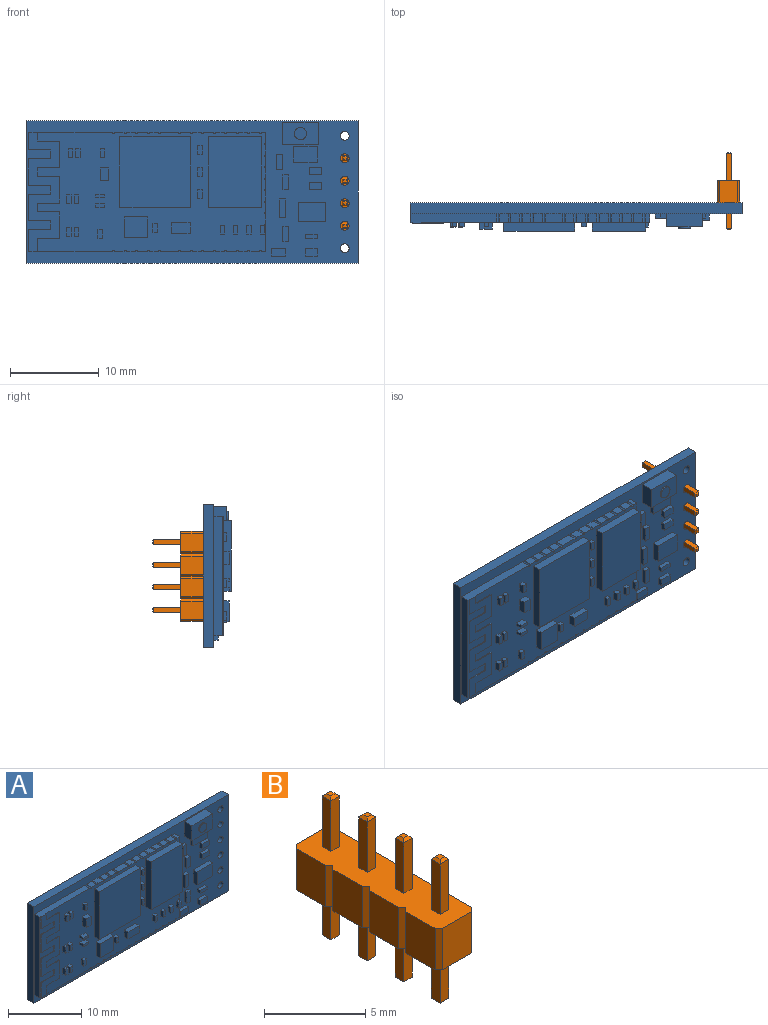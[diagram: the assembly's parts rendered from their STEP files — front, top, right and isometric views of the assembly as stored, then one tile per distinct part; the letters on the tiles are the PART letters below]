
ASSEMBLY  parts=2 mates=1
PART A: 290 faces, bbox 37.5x3.2x16.1 mm
  f0: plane 2.91x1mm, normal (1,0,0), area 2.9mm2, adj f34,f35,f43,f283
  f1: plane 1x1mm, normal (1,0,0), area 1mm2, adj f34,f35,f282,f283
  f2: plane 1x1mm, normal (1,0,0), area 1mm2, adj f34,f35,f281,f282
  f3: plane 1x1mm, normal (1,0,0), area 1mm2, adj f34,f35,f280,f281
  f4: plane 1x1mm, normal (1,0,0), area 1mm2, adj f34,f35,f279,f280
  f5: plane 1x1mm, normal (1,0,0), area 1mm2, adj f34,f35,f278,f279
  f6: plane 1x1mm, normal (1,0,0), area 1mm2, adj f34,f35,f277,f278
  f7: plane 1x1mm, normal (1,0,0), area 1mm2, adj f34,f35,f276,f277
  f8: plane 1x1mm, normal (0,0,-1), area 1mm2, adj f34,f35,f274,f275
  f9: plane 1x1mm, normal (0,0,-1), area 1mm2, adj f34,f35,f273,f274
  f10: plane 1x1mm, normal (0,0,-1), area 1mm2, adj f34,f35,f272,f273
  f11: plane 1x1mm, normal (0,0,-1), area 1mm2, adj f34,f35,f271,f272
  f12: plane 1x1mm, normal (0,0,-1), area 1mm2, adj f34,f35,f270,f271
  f13: plane 1x1mm, normal (0,0,-1), area 1mm2, adj f34,f35,f269,f270
  f14: plane 1x1mm, normal (0,0,-1), area 1mm2, adj f34,f35,f268,f269
  f15: plane 1.96x1mm, normal (0,0,-1), area 2mm2, adj f34,f35,f267,f268
  f16: plane 1x1mm, normal (0,0,-1), area 1mm2, adj f34,f35,f266,f267
  f17: plane 1x1mm, normal (0,0,-1), area 1mm2, adj f34,f35,f265,f266
  f18: plane 1x1mm, normal (0,0,-1), area 1mm2, adj f34,f35,f264,f265
  f19: plane 1x1mm, normal (0,0,-1), area 1mm2, adj f34,f35,f263,f264
  f20: plane 9.67x1.1mm, normal (0,0,-1), area 9.8mm2, adj f34,f35,f36,f42,f46,f71,f72,f263
  f21: plane 1x1mm, normal (0,0,1), area 1mm2, adj f34,f35,f261,f262
  f22: plane 1x1mm, normal (0,0,1), area 1mm2, adj f34,f35,f260,f261
  f23: plane 1x1mm, normal (0,0,1), area 1mm2, adj f34,f35,f259,f260
  f24: plane 1x1mm, normal (0,0,1), area 1mm2, adj f34,f35,f258,f259
  f25: plane 1.96x1mm, normal (0,0,1), area 2mm2, adj f34,f35,f257,f258
  f26: plane 1x1mm, normal (0,0,1), area 1mm2, adj f34,f35,f256,f257
  f27: plane 1x1mm, normal (0,0,1), area 1mm2, adj f34,f35,f255,f256
  f28: plane 1x1mm, normal (0,0,1), area 1mm2, adj f34,f35,f254,f255
  f29: plane 1x1mm, normal (0,0,1), area 1mm2, adj f34,f35,f253,f254
  f30: plane 1x1mm, normal (0,0,1), area 1mm2, adj f34,f35,f252,f253
  f31: plane 1x1mm, normal (0,0,1), area 1mm2, adj f34,f35,f251,f252
  f32: plane 1x1mm, normal (0,0,1), area 1mm2, adj f34,f35,f250,f251
  f33: plane 1x0.5mm, normal (0,0,1), area 0.5mm2, adj f34,f35,f44,f250
  f34: plane 37.5x16.1mm, normal (0,-1,0), area 203.9mm2, adj f0,f1,f2,f3,f4,f5,f6,f7
  f35: plane 25.8x13.5mm, normal (0,-1,0), area 194mm2, adj f0,f1,f2,f3,f4,f5,f6,f7
  f36: plane 13.5x2.7mm, normal (0,-1,0), area 10.2mm2, adj f20,f42,f45,f59,f60,f61,f62,f63
  f37: plane 16.1x1.2mm, normal (-1,0,0), area 19.3mm2, adj f34,f38,f40,f41
  f38: plane 37.5x1.2mm, normal (0,0,-1), area 45mm2, adj f34,f37,f39,f41
  f39: plane 16.1x1.2mm, normal (1,0,0), area 19.3mm2, adj f34,f38,f40,f41
  f40: plane 37.5x1.2mm, normal (0,0,1), area 45mm2, adj f34,f37,f39,f41
  f41: plane 37.5x16.1mm, normal (0,1,0), area 599mm2, adj f37,f38,f39,f40,f284,f285,f286,f287
  f42: plane 13.5x1mm, normal (-1,0,0), area 13.5mm2, adj f20,f34,f36,f45
  f43: plane 1x0.5mm, normal (0,0,-1), area 0.5mm2, adj f0,f34,f35,f275
  f44: plane 1.2x1mm, normal (1,0,0), area 1.2mm2, adj f33,f34,f35,f276
  f45: plane 9.67x1.1mm, normal (0,0,1), area 9.8mm2, adj f34,f35,f36,f42,f58,f59,f72,f262
  f46: plane 1.5x0.1mm, normal (1,0,0), area 0.1mm2, adj f20,f35,f47,f72
  f47: plane 2.5x0.1mm, normal (0,0,-1), area 0.2mm2, adj f35,f46,f48,f72
  f48: plane 3x0.1mm, normal (1,0,0), area 0.3mm2, adj f35,f47,f49,f72
  f49: plane 2.5x0.1mm, normal (0,0,1), area 0.2mm2, adj f35,f48,f50,f72
  f50: plane 1x0.1mm, normal (1,0,0), area 0.1mm2, adj f35,f49,f51,f72
  f51: plane 2.5x0.1mm, normal (0,0,-1), area 0.2mm2, adj f35,f50,f52,f72
  f52: plane 3x0.1mm, normal (1,0,0), area 0.3mm2, adj f35,f51,f53,f72
  f53: plane 2.5x0.1mm, normal (0,0,1), area 0.2mm2, adj f35,f52,f54,f72
  f54: plane 1x0.1mm, normal (1,0,0), area 0.1mm2, adj f35,f53,f55,f72
  f55: plane 2.5x0.1mm, normal (0,0,-1), area 0.2mm2, adj f35,f54,f56,f72
  f56: plane 3x0.1mm, normal (1,0,0), area 0.3mm2, adj f35,f55,f57,f72
  f57: plane 2.5x0.1mm, normal (0,0,1), area 0.2mm2, adj f35,f56,f58,f72
  f58: plane 1x0.1mm, normal (1,0,0), area 0.1mm2, adj f35,f45,f57,f72
  f59: plane 2x0.1mm, normal (-1,0,0), area 0.2mm2, adj f36,f45,f60,f72
  f60: plane 2.5x0.1mm, normal (0,0,-1), area 0.2mm2, adj f36,f59,f61,f72
  f61: plane 1x0.1mm, normal (-1,0,0), area 0.1mm2, adj f36,f60,f62,f72
  f62: plane 2.5x0.1mm, normal (0,0,1), area 0.2mm2, adj f36,f61,f63,f72
  f63: plane 3x0.1mm, normal (-1,0,0), area 0.3mm2, adj f36,f62,f64,f72
  f64: plane 2.5x0.1mm, normal (0,0,-1), area 0.2mm2, adj f36,f63,f65,f72
  f65: plane 1x0.1mm, normal (-1,0,0), area 0.1mm2, adj f36,f64,f66,f72
  f66: plane 2.5x0.1mm, normal (0,0,1), area 0.2mm2, adj f36,f65,f67,f72
  f67: plane 3x0.1mm, normal (-1,0,0), area 0.3mm2, adj f36,f66,f68,f72
  f68: plane 2.5x0.1mm, normal (0,0,-1), area 0.2mm2, adj f36,f67,f69,f72
  f69: plane 1x0.1mm, normal (-1,0,0), area 0.1mm2, adj f36,f68,f70,f72
  f70: plane 2.5x0.1mm, normal (0,0,1), area 0.2mm2, adj f36,f69,f71,f72
  f71: plane 2.5x0.1mm, normal (-1,0,0), area 0.2mm2, adj f20,f36,f70,f72
  f72: plane 13.5x3.5mm, normal (0,-1,0), area 28.5mm2, adj f20,f45,f46,f47,f48,f49,f50,f51
  f73: plane 2.5x1.5mm, normal (-1,0,0), area 3.8mm2, adj f34,f74,f76,f77
  f74: plane 4x1.5mm, normal (0,0,-1), area 6mm2, adj f34,f73,f75,f77
  f75: plane 2.5x1.5mm, normal (1,0,0), area 3.8mm2, adj f34,f74,f76,f77
  f76: plane 4x1.5mm, normal (0,0,1), area 6mm2, adj f34,f73,f75,f77
  f77: plane 4x2.5mm, normal (0,-1,0), area 8.5mm2, adj f73,f74,f75,f76,f78
  f78: cylinder r=0.69mm len=1.39mm, axis (0,1,0), area 0.9mm2, adj f77,f79
  f79: plane 1.39x1.39mm, normal (0,-1,0), area 1.5mm2, adj f78
  f80: plane 8x1mm, normal (1,0,0), area 8mm2, adj f35,f81,f83,f84
  f81: plane 6x1mm, normal (0,0,1), area 6mm2, adj f35,f80,f82,f84
  f82: plane 8x1mm, normal (-1,0,0), area 8mm2, adj f35,f81,f83,f84
  f83: plane 6x1mm, normal (0,0,-1), area 6mm2, adj f35,f80,f82,f84
  f84: plane 8x6mm, normal (0,-1,0), area 48mm2, adj f80,f81,f82,f83
  f85: plane 8x1mm, normal (1,0,0), area 8mm2, adj f35,f86,f88,f89
  f86: plane 8x1mm, normal (0,0,1), area 8mm2, adj f35,f85,f87,f89
  f87: plane 8x1mm, normal (-1,0,0), area 8mm2, adj f35,f86,f88,f89
  f88: plane 8x1mm, normal (0,0,-1), area 8mm2, adj f35,f85,f87,f89
  f89: plane 8x8mm, normal (0,-1,0), area 64mm2, adj f85,f86,f87,f88
  f90: plane 1x0.5mm, normal (-1,0,0), area 0.5mm2, adj f35,f91,f93,f94
  f91: plane 0.5x0.5mm, normal (0,0,-1), area 0.3mm2, adj f35,f90,f92,f94
  f92: plane 1x0.5mm, normal (1,0,0), area 0.5mm2, adj f35,f91,f93,f94
  f93: plane 0.5x0.5mm, normal (0,0,1), area 0.3mm2, adj f35,f90,f92,f94
  f94: plane 1x0.5mm, normal (0,-1,0), area 0.5mm2, adj f90,f91,f92,f93
  f95: plane 1x0.5mm, normal (-1,0,0), area 0.5mm2, adj f35,f96,f98,f99
  f96: plane 0.5x0.5mm, normal (0,0,-1), area 0.3mm2, adj f35,f95,f97,f99
  f97: plane 1x0.5mm, normal (1,0,0), area 0.5mm2, adj f35,f96,f98,f99
  f98: plane 0.5x0.5mm, normal (0,0,1), area 0.3mm2, adj f35,f95,f97,f99
  f99: plane 1x0.5mm, normal (0,-1,0), area 0.5mm2, adj f95,f96,f97,f98
  f100: plane 1x0.5mm, normal (-1,0,0), area 0.5mm2, adj f35,f101,f103,f104
  f101: plane 0.5x0.5mm, normal (0,0,-1), area 0.3mm2, adj f35,f100,f102,f104
  f102: plane 1x0.5mm, normal (1,0,0), area 0.5mm2, adj f35,f101,f103,f104
  f103: plane 0.5x0.5mm, normal (0,0,1), area 0.3mm2, adj f35,f100,f102,f104
  f104: plane 1x0.5mm, normal (0,-1,0), area 0.5mm2, adj f100,f101,f102,f103
  f105: plane 1x0.5mm, normal (-1,0,0), area 0.5mm2, adj f35,f106,f108,f109
  f106: plane 0.5x0.5mm, normal (0,0,-1), area 0.2mm2, adj f35,f105,f107,f109
  f107: plane 1x0.5mm, normal (1,0,0), area 0.5mm2, adj f35,f106,f108,f109
  f108: plane 0.5x0.5mm, normal (0,0,1), area 0.2mm2, adj f35,f105,f107,f109
  f109: plane 1x0.5mm, normal (0,-1,0), area 0.5mm2, adj f105,f106,f107,f108
  f110: plane 1x0.5mm, normal (-1,0,0), area 0.5mm2, adj f35,f111,f113,f114
  f111: plane 0.5x0.5mm, normal (0,0,-1), area 0.2mm2, adj f35,f110,f112,f114
  f112: plane 1x0.5mm, normal (1,0,0), area 0.5mm2, adj f35,f111,f113,f114
  f113: plane 0.5x0.5mm, normal (0,0,1), area 0.2mm2, adj f35,f110,f112,f114
  f114: plane 1x0.5mm, normal (0,-1,0), area 0.5mm2, adj f110,f111,f112,f113
  f115: plane 1x0.5mm, normal (-1,0,0), area 0.5mm2, adj f35,f116,f118,f119
  f116: plane 0.5x0.5mm, normal (0,0,-1), area 0.2mm2, adj f35,f115,f117,f119
  f117: plane 1x0.5mm, normal (1,0,0), area 0.5mm2, adj f35,f116,f118,f119
  f118: plane 0.5x0.5mm, normal (0,0,1), area 0.2mm2, adj f35,f115,f117,f119
  f119: plane 1x0.5mm, normal (0,-1,0), area 0.5mm2, adj f115,f116,f117,f118
  f120: plane 1x0.5mm, normal (-1,0,0), area 0.5mm2, adj f35,f121,f123,f124
  f121: plane 0.5x0.5mm, normal (0,0,-1), area 0.2mm2, adj f35,f120,f122,f124
  f122: plane 1x0.5mm, normal (1,0,0), area 0.5mm2, adj f35,f121,f123,f124
  f123: plane 0.5x0.5mm, normal (0,0,1), area 0.2mm2, adj f35,f120,f122,f124
  f124: plane 1x0.5mm, normal (0,-1,0), area 0.5mm2, adj f120,f121,f122,f123
  f125: plane 1x0.5mm, normal (-1,0,0), area 0.5mm2, adj f35,f126,f128,f129
  f126: plane 0.5x0.5mm, normal (0,0,-1), area 0.3mm2, adj f35,f125,f127,f129
  f127: plane 1x0.5mm, normal (1,0,0), area 0.5mm2, adj f35,f126,f128,f129
  f128: plane 0.5x0.5mm, normal (0,0,1), area 0.3mm2, adj f35,f125,f127,f129
  f129: plane 1x0.5mm, normal (0,-1,0), area 0.5mm2, adj f125,f126,f127,f128
  f130: plane 1x0.5mm, normal (-1,0,0), area 0.5mm2, adj f35,f131,f133,f134
  f131: plane 0.5x0.5mm, normal (0,0,-1), area 0.3mm2, adj f35,f130,f132,f134
  f132: plane 1x0.5mm, normal (1,0,0), area 0.5mm2, adj f35,f131,f133,f134
  f133: plane 0.5x0.5mm, normal (0,0,1), area 0.3mm2, adj f35,f130,f132,f134
  f134: plane 1x0.5mm, normal (0,-1,0), area 0.5mm2, adj f130,f131,f132,f133
  f135: plane 1x0.5mm, normal (-1,0,0), area 0.5mm2, adj f35,f136,f138,f139
  f136: plane 0.5x0.5mm, normal (0,0,-1), area 0.3mm2, adj f35,f135,f137,f139
  f137: plane 1x0.5mm, normal (1,0,0), area 0.5mm2, adj f35,f136,f138,f139
  f138: plane 0.5x0.5mm, normal (0,0,1), area 0.3mm2, adj f35,f135,f137,f139
  f139: plane 1x0.5mm, normal (0,-1,0), area 0.5mm2, adj f135,f136,f137,f138
  f140: plane 1x0.5mm, normal (1,0,0), area 0.5mm2, adj f35,f141,f143,f144
  f141: plane 0.5x0.5mm, normal (0,0,1), area 0.3mm2, adj f35,f140,f142,f144
  f142: plane 1x0.5mm, normal (-1,0,0), area 0.5mm2, adj f35,f141,f143,f144
  f143: plane 0.5x0.5mm, normal (0,0,-1), area 0.3mm2, adj f35,f140,f142,f144
  f144: plane 1x0.5mm, normal (0,-1,0), area 0.5mm2, adj f140,f141,f142,f143
  f145: plane 1x0.5mm, normal (-1,0,0), area 0.5mm2, adj f35,f146,f148,f149
  f146: plane 0.5x0.5mm, normal (0,0,-1), area 0.3mm2, adj f35,f145,f147,f149
  f147: plane 1x0.5mm, normal (1,0,0), area 0.5mm2, adj f35,f146,f148,f149
  f148: plane 0.5x0.5mm, normal (0,0,1), area 0.3mm2, adj f35,f145,f147,f149
  f149: plane 1x0.5mm, normal (0,-1,0), area 0.5mm2, adj f145,f146,f147,f148
  f150: plane 1x0.5mm, normal (-1,0,0), area 0.5mm2, adj f35,f151,f153,f154
  f151: plane 0.5x0.5mm, normal (0,0,-1), area 0.3mm2, adj f35,f150,f152,f154
  f152: plane 1x0.5mm, normal (1,0,0), area 0.5mm2, adj f35,f151,f153,f154
  f153: plane 0.5x0.5mm, normal (0,0,1), area 0.3mm2, adj f35,f150,f152,f154
  f154: plane 1x0.5mm, normal (0,-1,0), area 0.5mm2, adj f150,f151,f152,f153
  f155: plane 1x0.5mm, normal (-1,0,0), area 0.5mm2, adj f35,f156,f158,f159
  f156: plane 0.5x0.5mm, normal (0,0,-1), area 0.3mm2, adj f35,f155,f157,f159
  f157: plane 1x0.5mm, normal (1,0,0), area 0.5mm2, adj f35,f156,f158,f159
  f158: plane 0.5x0.5mm, normal (0,0,1), area 0.3mm2, adj f35,f155,f157,f159
  f159: plane 1x0.5mm, normal (0,-1,0), area 0.5mm2, adj f155,f156,f157,f158
  f160: plane 1x0.5mm, normal (-1,0,0), area 0.5mm2, adj f35,f161,f163,f164
  f161: plane 0.5x0.5mm, normal (0,0,-1), area 0.3mm2, adj f35,f160,f162,f164
  f162: plane 1x0.5mm, normal (1,0,0), area 0.5mm2, adj f35,f161,f163,f164
  f163: plane 0.5x0.5mm, normal (0,0,1), area 0.3mm2, adj f35,f160,f162,f164
  f164: plane 1x0.5mm, normal (0,-1,0), area 0.5mm2, adj f160,f161,f162,f163
  f165: plane 1x0.5mm, normal (-1,0,0), area 0.5mm2, adj f35,f166,f168,f169
  f166: plane 0.5x0.5mm, normal (0,0,-1), area 0.2mm2, adj f35,f165,f167,f169
  f167: plane 1x0.5mm, normal (1,0,0), area 0.5mm2, adj f35,f166,f168,f169
  f168: plane 0.5x0.5mm, normal (0,0,1), area 0.2mm2, adj f35,f165,f167,f169
  f169: plane 1x0.5mm, normal (0,-1,0), area 0.5mm2, adj f165,f166,f167,f168
  f170: plane 2.37x0.75mm, normal (-1,0,0), area 1.8mm2, adj f35,f171,f173,f174
  f171: plane 2.6x0.75mm, normal (0,0,-1), area 2mm2, adj f35,f170,f172,f174
  f172: plane 2.37x0.75mm, normal (1,0,0), area 1.8mm2, adj f35,f171,f173,f174
  f173: plane 2.6x0.75mm, normal (0,0,1), area 2mm2, adj f35,f170,f172,f174
  f174: plane 2.6x2.37mm, normal (0,-1,0), area 6.2mm2, adj f170,f171,f172,f173
  f175: plane 0.75x0.37mm, normal (-1,0,0), area 0.3mm2, adj f35,f176,f178,f179
  f176: plane 0.98x0.75mm, normal (0,0,-1), area 0.7mm2, adj f35,f175,f177,f179
  f177: plane 0.75x0.37mm, normal (1,0,0), area 0.3mm2, adj f35,f176,f178,f179
  f178: plane 0.98x0.75mm, normal (0,0,1), area 0.7mm2, adj f35,f175,f177,f179
  f179: plane 0.98x0.37mm, normal (0,-1,0), area 0.4mm2, adj f175,f176,f177,f178
  f180: plane 1.17x0.75mm, normal (-1,0,0), area 0.9mm2, adj f35,f181,f183,f184
  f181: plane 2.14x0.75mm, normal (0,0,-1), area 1.6mm2, adj f35,f180,f182,f184
  f182: plane 1.17x0.75mm, normal (1,0,0), area 0.9mm2, adj f35,f181,f183,f184
  f183: plane 2.14x0.75mm, normal (0,0,1), area 1.6mm2, adj f35,f180,f182,f184
  f184: plane 2.14x1.17mm, normal (0,-1,0), area 2.5mm2, adj f180,f181,f182,f183
  f185: plane 0.75x0.33mm, normal (-1,0,0), area 0.3mm2, adj f35,f186,f188,f189
  f186: plane 0.98x0.75mm, normal (0,0,-1), area 0.7mm2, adj f35,f185,f187,f189
  f187: plane 0.75x0.33mm, normal (1,0,0), area 0.3mm2, adj f35,f186,f188,f189
  f188: plane 0.98x0.75mm, normal (0,0,1), area 0.7mm2, adj f35,f185,f187,f189
  f189: plane 0.98x0.33mm, normal (0,-1,0), area 0.3mm2, adj f185,f186,f187,f188
  f190: plane 1.46x0.75mm, normal (-1,0,0), area 1.1mm2, adj f35,f191,f193,f194
  f191: plane 0.94x0.75mm, normal (0,0,-1), area 0.7mm2, adj f35,f190,f192,f194
  f192: plane 1.46x0.75mm, normal (1,0,0), area 1.1mm2, adj f35,f191,f193,f194
  f193: plane 0.94x0.75mm, normal (0,0,1), area 0.7mm2, adj f35,f190,f192,f194
  f194: plane 1.46x0.94mm, normal (0,-1,0), area 1.4mm2, adj f190,f191,f192,f193
  f195: plane 1.74x0.5mm, normal (-1,0,0), area 0.9mm2, adj f34,f196,f198,f199
  f196: plane 2.71x0.5mm, normal (0,0,-1), area 1.4mm2, adj f34,f195,f197,f199
  f197: plane 1.74x0.5mm, normal (1,0,0), area 0.9mm2, adj f34,f196,f198,f199
  f198: plane 2.71x0.5mm, normal (0,0,1), area 1.4mm2, adj f34,f195,f197,f199
  f199: plane 2.71x1.74mm, normal (0,-1,0), area 4.7mm2, adj f195,f196,f197,f198
  f200: plane 1.73x0.5mm, normal (-1,0,0), area 0.9mm2, adj f34,f201,f203,f204
  f201: plane 0.72x0.5mm, normal (0,0,-1), area 0.4mm2, adj f34,f200,f202,f204
  f202: plane 1.73x0.5mm, normal (1,0,0), area 0.9mm2, adj f34,f201,f203,f204
  f203: plane 0.72x0.5mm, normal (0,0,1), area 0.4mm2, adj f34,f200,f202,f204
  f204: plane 1.73x0.72mm, normal (0,-1,0), area 1.2mm2, adj f200,f201,f202,f203
  f205: plane 1.69x0.5mm, normal (-1,0,0), area 0.8mm2, adj f34,f206,f208,f209
  f206: plane 0.65x0.5mm, normal (0,0,-1), area 0.3mm2, adj f34,f205,f207,f209
  f207: plane 1.69x0.5mm, normal (1,0,0), area 0.8mm2, adj f34,f206,f208,f209
  f208: plane 0.65x0.5mm, normal (0,0,1), area 0.3mm2, adj f34,f205,f207,f209
  f209: plane 1.69x0.65mm, normal (0,-1,0), area 1.1mm2, adj f205,f206,f207,f208
  f210: plane 2.11x0.5mm, normal (-1,0,0), area 1.1mm2, adj f34,f211,f213,f214
  f211: plane 0.68x0.5mm, normal (0,0,-1), area 0.3mm2, adj f34,f210,f212,f214
  f212: plane 2.11x0.5mm, normal (1,0,0), area 1.1mm2, adj f34,f211,f213,f214
  f213: plane 0.68x0.5mm, normal (0,0,1), area 0.3mm2, adj f34,f210,f212,f214
  f214: plane 2.11x0.68mm, normal (0,-1,0), area 1.4mm2, adj f210,f211,f212,f213
  f215: plane 1.8x0.5mm, normal (-1,0,0), area 0.9mm2, adj f34,f216,f218,f219
  f216: plane 0.67x0.5mm, normal (0,0,-1), area 0.3mm2, adj f34,f215,f217,f219
  f217: plane 1.8x0.5mm, normal (1,0,0), area 0.9mm2, adj f34,f216,f218,f219
  f218: plane 0.67x0.5mm, normal (0,0,1), area 0.3mm2, adj f34,f215,f217,f219
  f219: plane 1.8x0.67mm, normal (0,-1,0), area 1.2mm2, adj f215,f216,f217,f218
  f220: plane 0.86x0.5mm, normal (-1,0,0), area 0.4mm2, adj f34,f221,f223,f224
  f221: plane 1.63x0.5mm, normal (0,0,-1), area 0.8mm2, adj f34,f220,f222,f224
  f222: plane 0.86x0.5mm, normal (1,0,0), area 0.4mm2, adj f34,f221,f223,f224
  f223: plane 1.63x0.5mm, normal (0,0,1), area 0.8mm2, adj f34,f220,f222,f224
  f224: plane 1.63x0.86mm, normal (0,-1,0), area 1.4mm2, adj f220,f221,f222,f223
  f225: plane 0.86x0.5mm, normal (-1,0,0), area 0.4mm2, adj f34,f226,f228,f229
  f226: plane 1.35x0.5mm, normal (0,0,-1), area 0.7mm2, adj f34,f225,f227,f229
  f227: plane 0.86x0.5mm, normal (1,0,0), area 0.4mm2, adj f34,f226,f228,f229
  f228: plane 1.35x0.5mm, normal (0,0,1), area 0.7mm2, adj f34,f225,f227,f229
  f229: plane 1.35x0.86mm, normal (0,-1,0), area 1.2mm2, adj f225,f226,f227,f228
  f230: plane 0.5x0.5mm, normal (-1,0,0), area 0.2mm2, adj f34,f231,f233,f234
  f231: plane 1.35x0.5mm, normal (0,0,-1), area 0.7mm2, adj f34,f230,f232,f234
  f232: plane 0.5x0.5mm, normal (1,0,0), area 0.2mm2, adj f34,f231,f233,f234
  f233: plane 1.35x0.5mm, normal (0,0,1), area 0.7mm2, adj f34,f230,f232,f234
  f234: plane 1.35x0.5mm, normal (0,-1,0), area 0.7mm2, adj f230,f231,f232,f233
  f235: plane 0.82x0.5mm, normal (-1,0,0), area 0.4mm2, adj f34,f236,f238,f239
  f236: plane 1.37x0.5mm, normal (0,0,-1), area 0.7mm2, adj f34,f235,f237,f239
  f237: plane 0.82x0.5mm, normal (1,0,0), area 0.4mm2, adj f34,f236,f238,f239
  f238: plane 1.37x0.5mm, normal (0,0,1), area 0.7mm2, adj f34,f235,f237,f239
  f239: plane 1.37x0.82mm, normal (0,-1,0), area 1.1mm2, adj f235,f236,f237,f238
  f240: plane 0.79x0.5mm, normal (-1,0,0), area 0.4mm2, adj f34,f241,f243,f244
  f241: plane 1.37x0.5mm, normal (0,0,-1), area 0.7mm2, adj f34,f240,f242,f244
  f242: plane 0.79x0.5mm, normal (1,0,0), area 0.4mm2, adj f34,f241,f243,f244
  f243: plane 1.37x0.5mm, normal (0,0,1), area 0.7mm2, adj f34,f240,f242,f244
  f244: plane 1.37x0.79mm, normal (0,-1,0), area 1.1mm2, adj f240,f241,f242,f243
  f245: plane 2.17x0.75mm, normal (-1,0,0), area 1.6mm2, adj f34,f246,f248,f249
  f246: plane 3.05x0.75mm, normal (0,0,-1), area 2.3mm2, adj f34,f245,f247,f249
  f247: plane 2.17x0.75mm, normal (1,0,0), area 1.6mm2, adj f34,f246,f248,f249
  f248: plane 3.05x0.75mm, normal (0,0,1), area 2.3mm2, adj f34,f245,f247,f249
  f249: plane 3.05x2.17mm, normal (0,-1,0), area 6.6mm2, adj f245,f246,f247,f248
  f250: cylinder r=0.15mm len=1mm, axis (0,-1,0), area 0.5mm2, adj f32,f33,f34,f35
  f251: cylinder r=0.15mm len=1mm, axis (0,-1,0), area 0.5mm2, adj f31,f32,f34,f35
  f252: cylinder r=0.15mm len=1mm, axis (0,-1,0), area 0.5mm2, adj f30,f31,f34,f35
  f253: cylinder r=0.15mm len=1mm, axis (0,-1,0), area 0.5mm2, adj f29,f30,f34,f35
  f254: cylinder r=0.15mm len=1mm, axis (0,-1,0), area 0.5mm2, adj f28,f29,f34,f35
  f255: cylinder r=0.15mm len=1mm, axis (0,-1,0), area 0.5mm2, adj f27,f28,f34,f35
  f256: cylinder r=0.15mm len=1mm, axis (0,-1,0), area 0.5mm2, adj f26,f27,f34,f35
  f257: cylinder r=0.15mm len=1mm, axis (0,-1,0), area 0.5mm2, adj f25,f26,f34,f35
  f258: cylinder r=0.15mm len=1mm, axis (0,-1,0), area 0.5mm2, adj f24,f25,f34,f35
  f259: cylinder r=0.15mm len=1mm, axis (0,-1,0), area 0.5mm2, adj f23,f24,f34,f35
  f260: cylinder r=0.15mm len=1mm, axis (0,-1,0), area 0.5mm2, adj f22,f23,f34,f35
  f261: cylinder r=0.15mm len=1mm, axis (0,-1,0), area 0.5mm2, adj f21,f22,f34,f35
  f262: cylinder r=0.15mm len=1mm, axis (0,-1,0), area 0.5mm2, adj f21,f34,f35,f45
  f263: cylinder r=0.15mm len=1mm, axis (0,-1,0), area 0.5mm2, adj f19,f20,f34,f35
  f264: cylinder r=0.15mm len=1mm, axis (0,-1,0), area 0.5mm2, adj f18,f19,f34,f35
  f265: cylinder r=0.15mm len=1mm, axis (0,-1,0), area 0.5mm2, adj f17,f18,f34,f35
  f266: cylinder r=0.15mm len=1mm, axis (0,-1,0), area 0.5mm2, adj f16,f17,f34,f35
  f267: cylinder r=0.15mm len=1mm, axis (0,-1,0), area 0.5mm2, adj f15,f16,f34,f35
  f268: cylinder r=0.15mm len=1mm, axis (0,-1,0), area 0.5mm2, adj f14,f15,f34,f35
  f269: cylinder r=0.15mm len=1mm, axis (0,-1,0), area 0.5mm2, adj f13,f14,f34,f35
  f270: cylinder r=0.15mm len=1mm, axis (0,-1,0), area 0.5mm2, adj f12,f13,f34,f35
  f271: cylinder r=0.15mm len=1mm, axis (0,-1,0), area 0.5mm2, adj f11,f12,f34,f35
  f272: cylinder r=0.15mm len=1mm, axis (0,-1,0), area 0.5mm2, adj f10,f11,f34,f35
  f273: cylinder r=0.15mm len=1mm, axis (0,-1,0), area 0.5mm2, adj f9,f10,f34,f35
  f274: cylinder r=0.15mm len=1mm, axis (0,-1,0), area 0.5mm2, adj f8,f9,f34,f35
  f275: cylinder r=0.15mm len=1mm, axis (0,-1,0), area 0.5mm2, adj f8,f34,f35,f43
  f276: cylinder r=0.15mm len=1mm, axis (0,-1,0), area 0.4mm2, adj f7,f34,f35,f44
  f277: cylinder r=0.15mm len=1mm, axis (0,-1,0), area 0.4mm2, adj f6,f7,f34,f35
  f278: cylinder r=0.15mm len=1mm, axis (0,-1,0), area 0.4mm2, adj f5,f6,f34,f35
  f279: cylinder r=0.15mm len=1mm, axis (0,-1,0), area 0.4mm2, adj f4,f5,f34,f35
  f280: cylinder r=0.15mm len=1mm, axis (0,-1,0), area 0.4mm2, adj f3,f4,f34,f35
  f281: cylinder r=0.15mm len=1mm, axis (0,-1,0), area 0.4mm2, adj f2,f3,f34,f35
  f282: cylinder r=0.15mm len=1mm, axis (0,-1,0), area 0.4mm2, adj f1,f2,f34,f35
  f283: cylinder r=0.15mm len=1mm, axis (0,-1,0), area 0.4mm2, adj f0,f1,f34,f35
  f284: cylinder r=0.5mm len=1.2mm, axis (0,-1,0), area 3.8mm2, adj f34,f41
  f285: cylinder r=0.5mm len=1.2mm, axis (0,-1,0), area 3.8mm2, adj f34,f41
  f286: cylinder r=0.5mm len=1.2mm, axis (0,-1,0), area 3.8mm2, adj f34,f41
  f287: cylinder r=0.5mm len=1.2mm, axis (0,-1,0), area 3.8mm2, adj f34,f41
  f288: cylinder r=0.5mm len=1.2mm, axis (0,-1,0), area 3.8mm2, adj f34,f41
  f289: cylinder r=0.5mm len=1.2mm, axis (0,-1,0), area 3.8mm2, adj f34,f41
PART B: 100 faces, bbox 2.5x10.2x8.7 mm
  f0: plane 2.5x2.04mm, normal (1,0,0), area 5.1mm2, adj f3,f4,f5,f8
  f1: plane 2.5x2.04mm, normal (-1,0,0), area 5.1mm2, adj f3,f4,f6,f7
  f2: plane 2.5x2.04mm, normal (0,-1,0), area 5.1mm2, adj f3,f4,f7,f8
  f3: plane 10.16x2.54mm, normal (0,0,1), area 23.9mm2, adj f0,f1,f2,f5,f6,f7,f8,f9
  f4: plane 10.16x2.54mm, normal (0,0,-1), area 23.9mm2, adj f0,f1,f2,f5,f6,f7,f8,f14
  f5: plane 2.5x0.25mm, normal (0.71,0.71,0), area 0.9mm2, adj f0,f3,f4,f32
  f6: plane 2.5x0.25mm, normal (-0.71,0.71,0), area 0.9mm2, adj f1,f3,f4,f31
  f7: plane 2.5x0.25mm, normal (-0.71,-0.71,0), area 0.9mm2, adj f1,f2,f3,f4
  f8: plane 2.5x0.25mm, normal (0.71,-0.71,0), area 0.9mm2, adj f0,f2,f3,f4
  f9: plane 3.05x0.6mm, normal (1,0,0), area 1.8mm2, adj f3,f10,f12,f22
  f10: plane 3.05x0.6mm, normal (0,1,0), area 1.8mm2, adj f3,f9,f11,f21
  f11: plane 3.05x0.6mm, normal (-1,0,0), area 1.8mm2, adj f3,f10,f12,f19
  f12: plane 3.05x0.6mm, normal (0,-1,0), area 1.8mm2, adj f3,f9,f11,f20
  f13: plane 0.3x0.3mm, normal (0,0,1), area 0.1mm2, adj f19,f20,f21,f22
  f14: plane 2.85x0.6mm, normal (1,0,0), area 1.7mm2, adj f4,f15,f17,f23
  f15: plane 2.85x0.6mm, normal (0,-1,0), area 1.7mm2, adj f4,f14,f16,f24
  f16: plane 2.85x0.6mm, normal (-1,0,0), area 1.7mm2, adj f4,f15,f17,f26
  f17: plane 2.85x0.6mm, normal (0,1,0), area 1.7mm2, adj f4,f14,f16,f25
  f18: plane 0.3x0.3mm, normal (0,0,-1), area 0.1mm2, adj f23,f24,f25,f26
  f19: plane 0.6x0.15mm, normal (-0.71,0,0.71), area 0.1mm2, adj f11,f13,f20,f21
  f20: plane 0.6x0.15mm, normal (0,-0.71,0.71), area 0.1mm2, adj f12,f13,f19,f22
  f21: plane 0.6x0.15mm, normal (0,0.71,0.71), area 0.1mm2, adj f10,f13,f19,f22
  f22: plane 0.6x0.15mm, normal (0.71,0,0.71), area 0.1mm2, adj f9,f13,f20,f21
  f23: plane 0.6x0.15mm, normal (0.71,0,-0.71), area 0.1mm2, adj f14,f18,f24,f25
  f24: plane 0.6x0.15mm, normal (0,-0.71,-0.71), area 0.1mm2, adj f15,f18,f23,f26
  f25: plane 0.6x0.15mm, normal (0,0.71,-0.71), area 0.1mm2, adj f17,f18,f23,f26
  f26: plane 0.6x0.15mm, normal (-0.71,0,-0.71), area 0.1mm2, adj f16,f18,f24,f25
  f27: plane 2.5x2.04mm, normal (1,0,0), area 5.1mm2, adj f3,f4,f29,f32
  f28: plane 2.5x2.04mm, normal (-1,0,0), area 5.1mm2, adj f3,f4,f30,f31
  f29: plane 2.5x0.25mm, normal (0.71,0.71,0), area 0.9mm2, adj f3,f4,f27,f56
  f30: plane 2.5x0.25mm, normal (-0.71,0.71,0), area 0.9mm2, adj f3,f4,f28,f55
  f31: plane 2.5x0.25mm, normal (-0.71,-0.71,0), area 0.9mm2, adj f3,f4,f6,f28
  f32: plane 2.5x0.25mm, normal (0.71,-0.71,0), area 0.9mm2, adj f3,f4,f5,f27
  f33: plane 3.05x0.6mm, normal (1,0,0), area 1.8mm2, adj f3,f34,f36,f46
  f34: plane 3.05x0.6mm, normal (0,1,0), area 1.8mm2, adj f3,f33,f35,f45
  f35: plane 3.05x0.6mm, normal (-1,0,0), area 1.8mm2, adj f3,f34,f36,f43
  f36: plane 3.05x0.6mm, normal (0,-1,0), area 1.8mm2, adj f3,f33,f35,f44
  f37: plane 0.3x0.3mm, normal (0,0,1), area 0.1mm2, adj f43,f44,f45,f46
  f38: plane 2.85x0.6mm, normal (1,0,0), area 1.7mm2, adj f4,f39,f41,f47
  f39: plane 2.85x0.6mm, normal (0,-1,0), area 1.7mm2, adj f4,f38,f40,f48
  f40: plane 2.85x0.6mm, normal (-1,0,0), area 1.7mm2, adj f4,f39,f41,f50
  f41: plane 2.85x0.6mm, normal (0,1,0), area 1.7mm2, adj f4,f38,f40,f49
  f42: plane 0.3x0.3mm, normal (0,0,-1), area 0.1mm2, adj f47,f48,f49,f50
  f43: plane 0.6x0.15mm, normal (-0.71,0,0.71), area 0.1mm2, adj f35,f37,f44,f45
  f44: plane 0.6x0.15mm, normal (0,-0.71,0.71), area 0.1mm2, adj f36,f37,f43,f46
  f45: plane 0.6x0.15mm, normal (0,0.71,0.71), area 0.1mm2, adj f34,f37,f43,f46
  f46: plane 0.6x0.15mm, normal (0.71,0,0.71), area 0.1mm2, adj f33,f37,f44,f45
  f47: plane 0.6x0.15mm, normal (0.71,0,-0.71), area 0.1mm2, adj f38,f42,f48,f49
  f48: plane 0.6x0.15mm, normal (0,-0.71,-0.71), area 0.1mm2, adj f39,f42,f47,f50
  f49: plane 0.6x0.15mm, normal (0,0.71,-0.71), area 0.1mm2, adj f41,f42,f47,f50
  f50: plane 0.6x0.15mm, normal (-0.71,0,-0.71), area 0.1mm2, adj f40,f42,f48,f49
  f51: plane 2.5x2.04mm, normal (1,0,0), area 5.1mm2, adj f3,f4,f53,f56
  f52: plane 2.5x2.04mm, normal (-1,0,0), area 5.1mm2, adj f3,f4,f54,f55
  f53: plane 2.5x0.25mm, normal (0.71,0.71,0), area 0.9mm2, adj f3,f4,f51,f81
  f54: plane 2.5x0.25mm, normal (-0.71,0.71,0), area 0.9mm2, adj f3,f4,f52,f80
  f55: plane 2.5x0.25mm, normal (-0.71,-0.71,0), area 0.9mm2, adj f3,f4,f30,f52
  f56: plane 2.5x0.25mm, normal (0.71,-0.71,0), area 0.9mm2, adj f3,f4,f29,f51
  f57: plane 3.05x0.6mm, normal (1,0,0), area 1.8mm2, adj f3,f58,f60,f70
  f58: plane 3.05x0.6mm, normal (0,1,0), area 1.8mm2, adj f3,f57,f59,f69
  f59: plane 3.05x0.6mm, normal (-1,0,0), area 1.8mm2, adj f3,f58,f60,f67
  f60: plane 3.05x0.6mm, normal (0,-1,0), area 1.8mm2, adj f3,f57,f59,f68
  f61: plane 0.3x0.3mm, normal (0,0,1), area 0.1mm2, adj f67,f68,f69,f70
  f62: plane 2.85x0.6mm, normal (1,0,0), area 1.7mm2, adj f4,f63,f65,f71
  f63: plane 2.85x0.6mm, normal (0,-1,0), area 1.7mm2, adj f4,f62,f64,f72
  f64: plane 2.85x0.6mm, normal (-1,0,0), area 1.7mm2, adj f4,f63,f65,f74
  f65: plane 2.85x0.6mm, normal (0,1,0), area 1.7mm2, adj f4,f62,f64,f73
  f66: plane 0.3x0.3mm, normal (0,0,-1), area 0.1mm2, adj f71,f72,f73,f74
  f67: plane 0.6x0.15mm, normal (-0.71,0,0.71), area 0.1mm2, adj f59,f61,f68,f69
  f68: plane 0.6x0.15mm, normal (0,-0.71,0.71), area 0.1mm2, adj f60,f61,f67,f70
  f69: plane 0.6x0.15mm, normal (0,0.71,0.71), area 0.1mm2, adj f58,f61,f67,f70
  f70: plane 0.6x0.15mm, normal (0.71,0,0.71), area 0.1mm2, adj f57,f61,f68,f69
  f71: plane 0.6x0.15mm, normal (0.71,0,-0.71), area 0.1mm2, adj f62,f66,f72,f73
  f72: plane 0.6x0.15mm, normal (0,-0.71,-0.71), area 0.1mm2, adj f63,f66,f71,f74
  f73: plane 0.6x0.15mm, normal (0,0.71,-0.71), area 0.1mm2, adj f65,f66,f71,f74
  f74: plane 0.6x0.15mm, normal (-0.71,0,-0.71), area 0.1mm2, adj f64,f66,f72,f73
  f75: plane 2.5x2.04mm, normal (1,0,0), area 5.1mm2, adj f3,f4,f78,f81
  f76: plane 2.5x2.04mm, normal (0,1,0), area 5.1mm2, adj f3,f4,f78,f79
  f77: plane 2.5x2.04mm, normal (-1,0,0), area 5.1mm2, adj f3,f4,f79,f80
  f78: plane 2.5x0.25mm, normal (0.71,0.71,0), area 0.9mm2, adj f3,f4,f75,f76
  f79: plane 2.5x0.25mm, normal (-0.71,0.71,0), area 0.9mm2, adj f3,f4,f76,f77
  f80: plane 2.5x0.25mm, normal (-0.71,-0.71,0), area 0.9mm2, adj f3,f4,f54,f77
  f81: plane 2.5x0.25mm, normal (0.71,-0.71,0), area 0.9mm2, adj f3,f4,f53,f75
  f82: plane 3.05x0.6mm, normal (1,0,0), area 1.8mm2, adj f3,f83,f85,f95
  f83: plane 3.05x0.6mm, normal (0,1,0), area 1.8mm2, adj f3,f82,f84,f94
  f84: plane 3.05x0.6mm, normal (-1,0,0), area 1.8mm2, adj f3,f83,f85,f92
  f85: plane 3.05x0.6mm, normal (0,-1,0), area 1.8mm2, adj f3,f82,f84,f93
  f86: plane 0.3x0.3mm, normal (0,0,1), area 0.1mm2, adj f92,f93,f94,f95
  f87: plane 2.85x0.6mm, normal (1,0,0), area 1.7mm2, adj f4,f88,f90,f96
  f88: plane 2.85x0.6mm, normal (0,-1,0), area 1.7mm2, adj f4,f87,f89,f97
  f89: plane 2.85x0.6mm, normal (-1,0,0), area 1.7mm2, adj f4,f88,f90,f99
  f90: plane 2.85x0.6mm, normal (0,1,0), area 1.7mm2, adj f4,f87,f89,f98
  f91: plane 0.3x0.3mm, normal (0,0,-1), area 0.1mm2, adj f96,f97,f98,f99
  f92: plane 0.6x0.15mm, normal (-0.71,0,0.71), area 0.1mm2, adj f84,f86,f93,f94
  f93: plane 0.6x0.15mm, normal (0,-0.71,0.71), area 0.1mm2, adj f85,f86,f92,f95
  f94: plane 0.6x0.15mm, normal (0,0.71,0.71), area 0.1mm2, adj f83,f86,f92,f95
  f95: plane 0.6x0.15mm, normal (0.71,0,0.71), area 0.1mm2, adj f82,f86,f93,f94
  f96: plane 0.6x0.15mm, normal (0.71,0,-0.71), area 0.1mm2, adj f87,f91,f97,f98
  f97: plane 0.6x0.15mm, normal (0,-0.71,-0.71), area 0.1mm2, adj f88,f91,f96,f99
  f98: plane 0.6x0.15mm, normal (0,0.71,-0.71), area 0.1mm2, adj f90,f91,f96,f99
  f99: plane 0.6x0.15mm, normal (-0.71,0,-0.71), area 0.1mm2, adj f89,f91,f97,f98
PLACE A t=(-12.5,6.74,-5.75)mm
PLACE B rot(axis=(-1,0,0),90deg) t=(23.45,6.74,6.06)mm
MATE fastened B.f4 <-> A.f285  axis (0,-1,0) through (23.5,6.74,-1.51)mm
